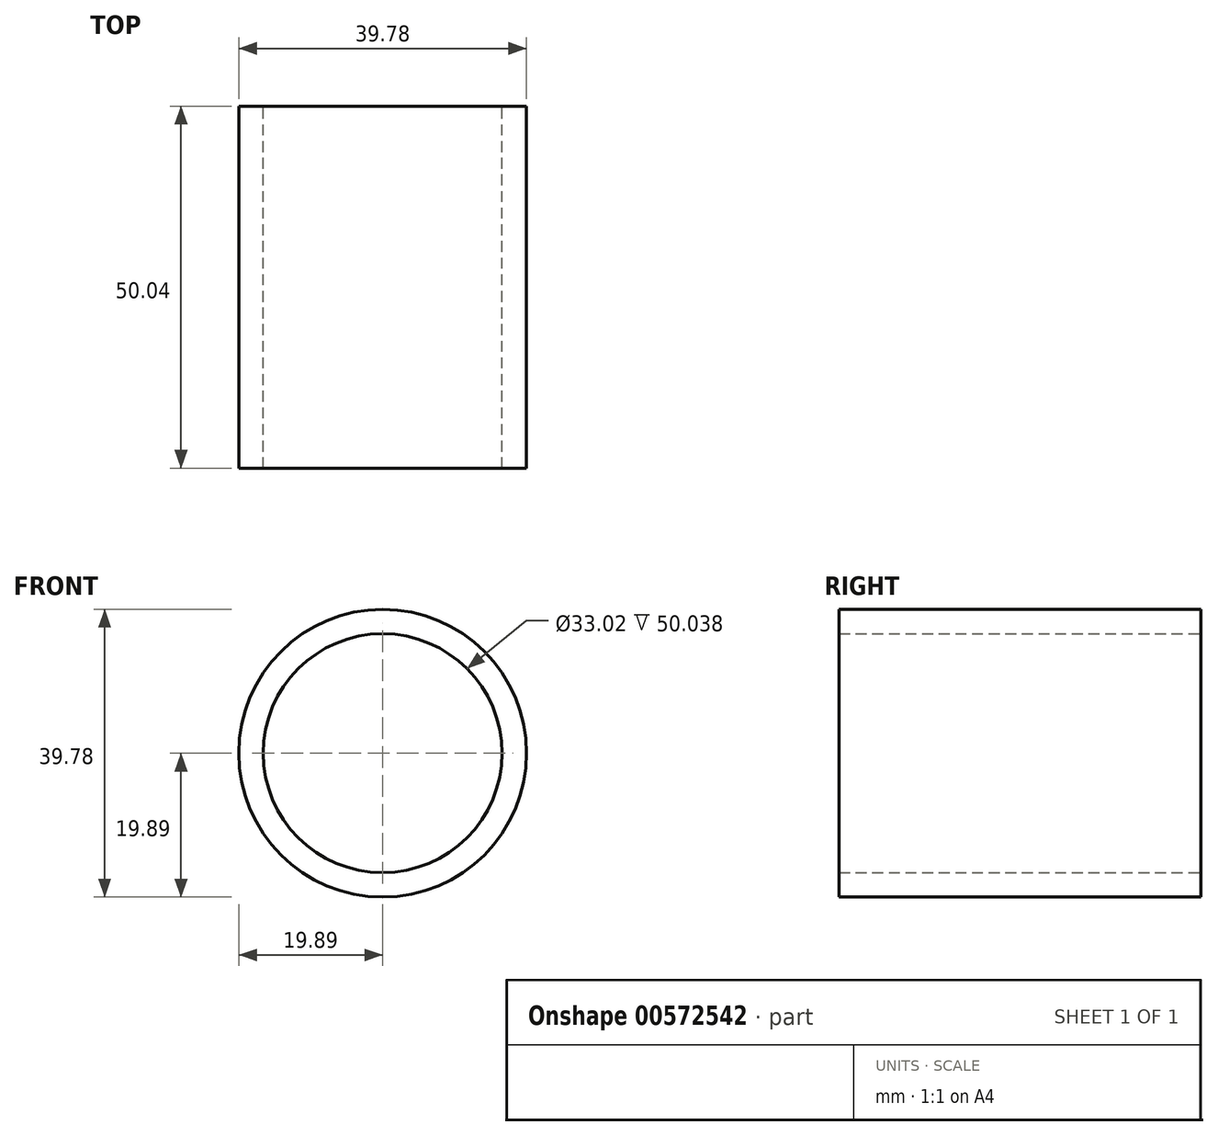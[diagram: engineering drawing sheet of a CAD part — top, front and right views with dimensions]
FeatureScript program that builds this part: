
annotation { "Feature Type Name" : "Feature", "Feature Type Description" : "" }
export const myFeature = defineFeature(function(context is Context, id is Id, definition is map)
    precondition{}
    {
        {
            var Q0;
            Q0=qCreatedBy(makeId("Front.planeOp"),FACE);
            var sketch = newSketch(context, id + "F0", { "sketchPlane" : qUnion([Q0])});
            skCircle(sketch, "E0", {"center": v(0, 0) * mm, "radius": 19.89 * mm});
            skSolve(sketch);
        }
        {
            var Q0;
            Q0=makeQuery(id+"F0.imprint","IMPRINT",FACE,{"disambiguationData":[TD([[makeQuery(id+"F0.imprint","IMPRINT",EDGE,{"derivedFrom":sQuery(id+"F0.wireOp",EDGE,"E0")}),1.0]])]});
            extrude(context, id + "F1", {"entities" : qUnion([Q0]), "depth" : 50.04 * mm, "offsetDistance" : 25.4 * mm});
        }
        {
            var Q0;
            Q0=sQuery(id+"F0.wireOp",VERTEX,"E0.center");
            var Q1;
            Q1=makeQuery(id+"F1.opExtrude","SWEPT_BODY",BODY,{"disambiguationData":[OSD([sQuery(id+"F0.wireOp",EDGE,"E0")])]});
            hole(context, id + "F2", {"style" : HoleStyle.SIMPLE, "endStyle" : HoleEndStyle.THROUGH, "oppositeDirection" : true, "holeDiameter" : 33.02 * mm, "isTappedThrough" : true, "tappedDepth" : 12.7 * mm, "tapClearance" : 3, "locations" : qUnion([Q0]), "scope" : qUnion([Q1])});
        }
    });
